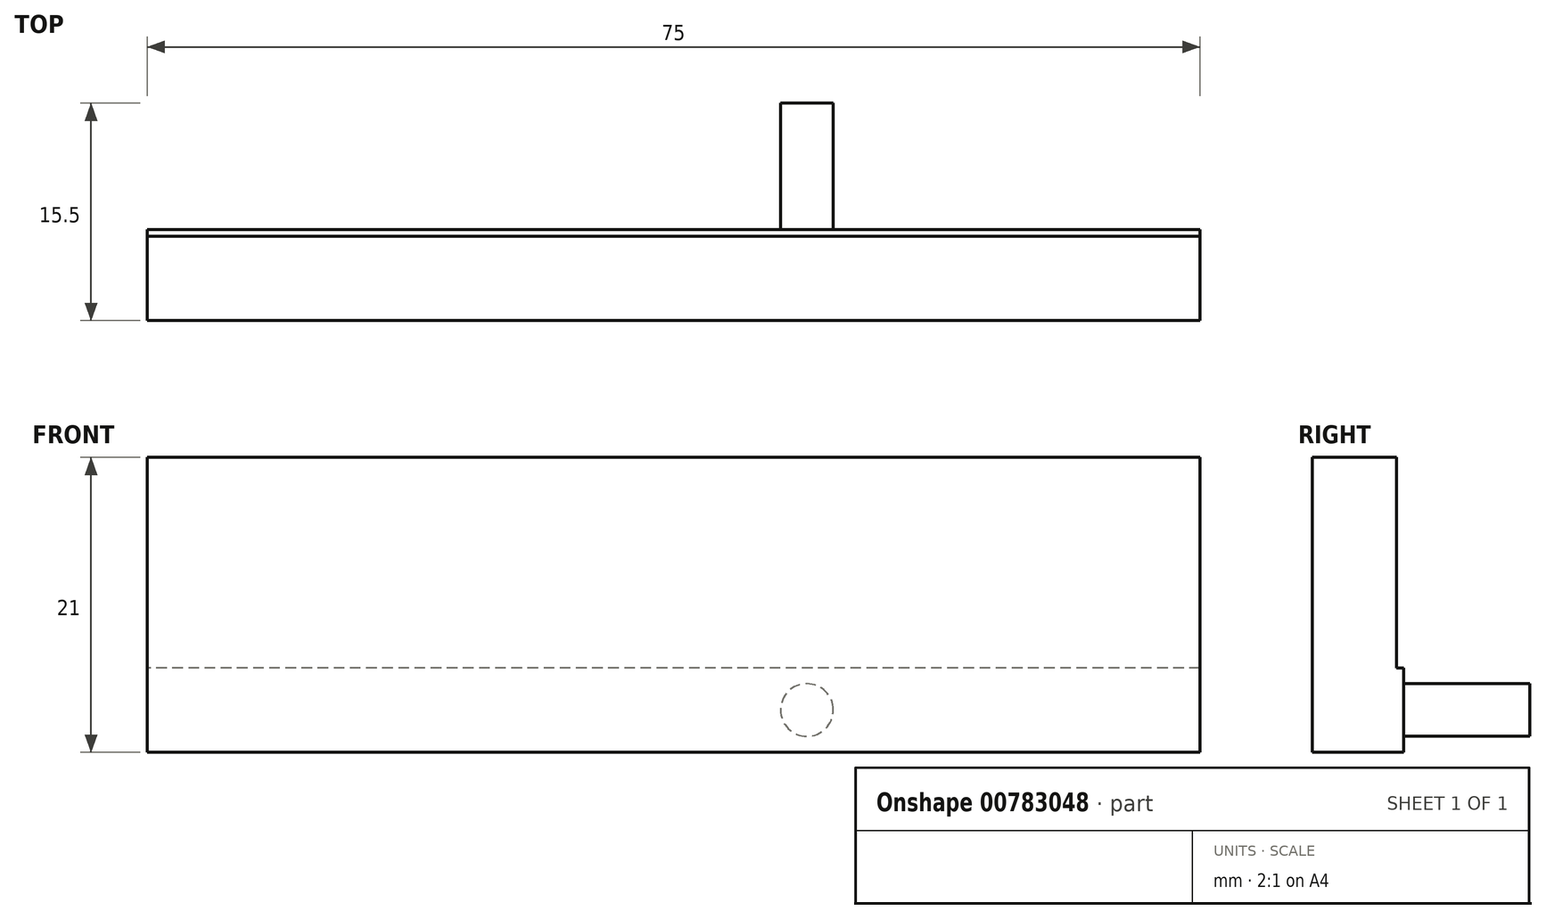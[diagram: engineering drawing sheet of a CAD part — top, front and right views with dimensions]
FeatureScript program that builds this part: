
annotation { "Feature Type Name" : "Feature", "Feature Type Description" : "" }
export const myFeature = defineFeature(function(context is Context, id is Id, definition is map)
    precondition{}
    {
        {
            var Q0;
            Q0=qCreatedBy(makeId("Right.planeOp"),FACE);
            var sketch = newSketch(context, id + "F0", { "sketchPlane" : qUnion([Q0])});
            skLineSegment(sketch, "E0", {"start": v(14.98, 53.88) * mm, "end": v(14.98, -37.12) * mm});
            skLineSegment(sketch, "E1", {"start": v(-0.52, -37.12) * mm, "end": v(14.98, -37.12) * mm});
            skLineSegment(sketch, "E2", {"start": v(-0.52, -37.12) * mm, "end": v(-0.52, -16.12) * mm});
            skLineSegment(sketch, "E3", {"start": v(5.48, -16.12) * mm, "end": v(5.48, -31.12) * mm});
            skLineSegment(sketch, "E4", {"start": v(5.48, -31.12) * mm, "end": v(8.98, -31.12) * mm});
            skLineSegment(sketch, "E5", {"start": v(8.98, -31.12) * mm, "end": v(8.98, 53.88) * mm});
            skLineSegment(sketch, "E6", {"start": v(8.98, 53.88) * mm, "end": v(14.98, 53.88) * mm});
            skLineSegment(sketch, "E7", {"start": v(-0.52, -16.12) * mm, "end": v(5.48, -16.12) * mm});
            skSolve(sketch);
        }
        {
            var Q0;
            Q0=makeQuery(id+"F0.imprint","IMPRINT",FACE,{"disambiguationData":[TD([[makeQuery(id+"F0.imprint","IMPRINT",EDGE,{"derivedFrom":sQuery(id+"F0.wireOp",EDGE,"E0")}),-1.0]])]});
            extrude(context, id + "F1", {"entities" : qUnion([Q0]), "depth" : 67 * mm, "offsetDistance" : 25 * mm});
        }
        {
            var Q0;
            Q0=makeQuery(id+"F1.opExtrude","CAP_FACE",FACE,{"disambiguationData":[OSD([sQuery(id+"F0.wireOp",EDGE,"E0"),sQuery(id+"F0.wireOp",EDGE,"E1"),sQuery(id+"F0.wireOp",EDGE,"E2"),sQuery(id+"F0.wireOp",EDGE,"E3"),sQuery(id+"F0.wireOp",EDGE,"E4"),sQuery(id+"F0.wireOp",EDGE,"E5"),sQuery(id+"F0.wireOp",EDGE,"E6"),sQuery(id+"F0.wireOp",EDGE,"E7")])],"isStart":false});
            var sketch = newSketch(context, id + "F2", { "sketchPlane" : qUnion([Q0])});
            skCircle(sketch, "E8", {"center": v(11.98, 43.88) * mm, "radius": 1.5 * mm});
            skCircle(sketch, "E9", {"center": v(11.98, 23.88) * mm, "radius": 1.5 * mm});
            skCircle(sketch, "E10.MirrorC", {"center": v(11.98, -27.12) * mm, "radius": 1.5 * mm});
            skCircle(sketch, "E11.MirrorC", {"center": v(11.98, -7.12) * mm, "radius": 1.5 * mm});
            skLineSegment(sketch, "E12", {"start": v(11.98, 43.88) * mm, "end": v(11.98, 53.88) * mm});
            skLineSegment(sketch, "E13", {"start": v(11.98, 43.88) * mm, "end": v(11.98, 23.88) * mm});
            skSolve(sketch);
        }
        {
            var Q0;
            Q0=makeQuery(id+"F2.imprint","IMPRINT",FACE,{"disambiguationData":[TD([[makeQuery(id+"F2.imprint","IMPRINT",EDGE,{"derivedFrom":sQuery(id+"F2.wireOp",EDGE,"E8")}),1.0]])]});
            var Q1;
            Q1=makeQuery(id+"F2.imprint","IMPRINT",FACE,{"disambiguationData":[TD([[makeQuery(id+"F2.imprint","IMPRINT",EDGE,{"derivedFrom":sQuery(id+"F2.wireOp",EDGE,"E9")}),1.0]])]});
            var Q2;
            Q2=makeQuery(id+"F2.imprint","IMPRINT",FACE,{"disambiguationData":[TD([[makeQuery(id+"F2.imprint","IMPRINT",EDGE,{"derivedFrom":sQuery(id+"F2.wireOp",EDGE,"E11.MirrorC")}),-1.0]])]});
            var Q3;
            Q3=makeQuery(id+"F2.imprint","IMPRINT",FACE,{"disambiguationData":[TD([[makeQuery(id+"F2.imprint","IMPRINT",EDGE,{"derivedFrom":sQuery(id+"F2.wireOp",EDGE,"E10.MirrorC")}),-1.0]])]});
            extrude(context, id + "F3", {"entities" : qUnion([Q0, Q1, Q2, Q3]), "operationType" : NewBodyOperationType.ADD, "depth" : 8 * mm, "offsetDistance" : 25 * mm});
        }
        {
            var Q0;
            Q0=makeQuery(id+"F1.opExtrude","CAP_FACE",FACE,{"disambiguationData":[OSD([sQuery(id+"F0.wireOp",EDGE,"E0"),sQuery(id+"F0.wireOp",EDGE,"E1"),sQuery(id+"F0.wireOp",EDGE,"E2"),sQuery(id+"F0.wireOp",EDGE,"E3"),sQuery(id+"F0.wireOp",EDGE,"E4"),sQuery(id+"F0.wireOp",EDGE,"E5"),sQuery(id+"F0.wireOp",EDGE,"E6"),sQuery(id+"F0.wireOp",EDGE,"E7")])],"isStart":true});
            var sketch = newSketch(context, id + "F4", { "sketchPlane" : qUnion([Q0])});
            skCircle(sketch, "E14", {"center": v(-18.48, 43.88) * mm, "radius": 1.88 * mm});
            skCircle(sketch, "E15", {"center": v(-18.48, 23.88) * mm, "radius": 1.88 * mm});
            skCircle(sketch, "E16.MirrorC", {"center": v(-18.48, -27.12) * mm, "radius": 1.88 * mm});
            skCircle(sketch, "E17.MirrorC", {"center": v(-18.48, -7.12) * mm, "radius": 1.88 * mm});
            skSolve(sketch);
        }
        {
            var Q0;
            Q0=makeQuery(id+"F4.imprint","IMPRINT",FACE,{"disambiguationData":[TD([[makeQuery(id+"F4.imprint","IMPRINT",EDGE,{"derivedFrom":sQuery(id+"F4.wireOp",EDGE,"E15")}),1.0]])]});
            var Q1;
            Q1=makeQuery(id+"F4.imprint","IMPRINT",FACE,{"disambiguationData":[TD([[makeQuery(id+"F4.imprint","IMPRINT",EDGE,{"derivedFrom":sQuery(id+"F4.wireOp",EDGE,"E14")}),1.0]])]});
            var Q2;
            Q2=makeQuery(id+"F4.imprint","IMPRINT",FACE,{"disambiguationData":[TD([[makeQuery(id+"F4.imprint","IMPRINT",EDGE,{"derivedFrom":sQuery(id+"F4.wireOp",EDGE,"E17.MirrorC")}),-1.0]])]});
            var Q3;
            Q3=makeQuery(id+"F4.imprint","IMPRINT",FACE,{"disambiguationData":[TD([[makeQuery(id+"F4.imprint","IMPRINT",EDGE,{"derivedFrom":sQuery(id+"F4.wireOp",EDGE,"E16.MirrorC")}),-1.0]])]});
            extrude(context, id + "F5", {"entities" : qUnion([Q0, Q1, Q2, Q3]), "operationType" : NewBodyOperationType.REMOVE, "oppositeDirection" : true, "depth" : 9 * mm, "offsetDistance" : 25 * mm});
        }
        {
            var Q0;
            Q0=makeQuery(id+"F1.opExtrude","SWEPT_FACE",FACE,{"disambiguationData":[OSD([sQuery(id+"F0.wireOp",EDGE,"E0")])]});
            var sketch = newSketch(context, id + "F6", { "sketchPlane" : qUnion([Q0])});
            skLineSegment(sketch, "E18", {"start": v(0, -37.12) * mm, "end": v(0, -34.12) * mm});
            skCircle(sketch, "E19", {"center": v(-20, -34.12) * mm, "radius": 1.88 * mm});
            skCircle(sketch, "E20.MirrorC", {"center": v(-47, -34.12) * mm, "radius": 1.88 * mm});
            skSolve(sketch);
        }
        {
            var Q0;
            Q0=makeQuery(id+"F6.imprint","IMPRINT",FACE,{"disambiguationData":[TD([[makeQuery(id+"F6.imprint","IMPRINT",EDGE,{"derivedFrom":sQuery(id+"F6.wireOp",EDGE,"E20.MirrorC")}),-1.0]])]});
            var Q1;
            Q1=makeQuery(id+"F6.imprint","IMPRINT",FACE,{"disambiguationData":[TD([[makeQuery(id+"F6.imprint","IMPRINT",EDGE,{"derivedFrom":sQuery(id+"F6.wireOp",EDGE,"064d96a8-f5e3-4a6a-84b9-f8e9dd95ac0b0.MirrorC")}),-1.0]])]});
            var Q2;
            Q2=makeQuery(id+"F6.imprint","IMPRINT",FACE,{"disambiguationData":[TD([[makeQuery(id+"F6.imprint","IMPRINT",EDGE,{"derivedFrom":sQuery(id+"F6.wireOp",EDGE,"sfNKTgSD-Wn5j-8V8k-rCBi-PUns8C3nGana")}),1.0]])]});
            var Q3;
            Q3=makeQuery(id+"F6.imprint","IMPRINT",FACE,{"disambiguationData":[TD([[makeQuery(id+"F6.imprint","IMPRINT",EDGE,{"derivedFrom":sQuery(id+"F6.wireOp",EDGE,"E19")}),1.0]])]});
            extrude(context, id + "F7", {"entities" : qUnion([Q0, Q1, Q2, Q3]), "operationType" : NewBodyOperationType.REMOVE, "oppositeDirection" : true, "depth" : 9 * mm, "offsetDistance" : 25 * mm});
        }
        {
            var Q0;
            Q0=makeQuery(id+"FH1SkS20bZ57wbL_1.boolean.opBoolean","MERGE",FACE,{"derivedFrom":[makeQuery(id+"F1.opExtrude","CAP_FACE",FACE,{"disambiguationData":[OSD([sQuery(id+"F0.wireOp",EDGE,"E0"),sQuery(id+"F0.wireOp",EDGE,"E1"),sQuery(id+"F0.wireOp",EDGE,"E2"),sQuery(id+"F0.wireOp",EDGE,"E3"),sQuery(id+"F0.wireOp",EDGE,"E4"),sQuery(id+"F0.wireOp",EDGE,"E5"),sQuery(id+"F0.wireOp",EDGE,"E6"),sQuery(id+"F0.wireOp",EDGE,"E7")])],"isStart":true}),makeQuery(id+"FH1SkS20bZ57wbL_1.opExtrude","SWEPT_FACE",FACE,{"disambiguationData":[OSD([sQuery(id+"FkPa33tsSXIzsnt_1.wireOp",EDGE,"F0n0BjA5-wISv-bXAu-321k-WS0dTKFj3dhw.left")])]})]});
            var sketch = newSketch(context, id + "F8", { "sketchPlane" : qUnion([Q0])});
            skLineSegment(sketch, "E21", {"start": v(-11.98, 53.88) * mm, "end": v(-11.98, 43.88) * mm});
            skLineSegment(sketch, "E22", {"start": v(-11.98, 43.88) * mm, "end": v(-11.98, 23.88) * mm});
            skCircle(sketch, "E23", {"center": v(-11.98, 43.88) * mm, "radius": 1.88 * mm});
            skCircle(sketch, "E24", {"center": v(-11.98, 23.88) * mm, "radius": 1.88 * mm});
            skCircle(sketch, "E25.MirrorC", {"center": v(-11.98, -27.12) * mm, "radius": 1.88 * mm});
            skCircle(sketch, "E26.MirrorC", {"center": v(-11.98, -7.12) * mm, "radius": 1.88 * mm});
            skSolve(sketch);
        }
        {
            var Q0;
            Q0=qSketchRegion(id+"F8",true);
            extrude(context, id + "F9", {"entities" : qUnion([Q0]), "operationType" : NewBodyOperationType.REMOVE, "oppositeDirection" : true, "depth" : 9 * mm, "offsetDistance" : 25 * mm});
        }
    });
